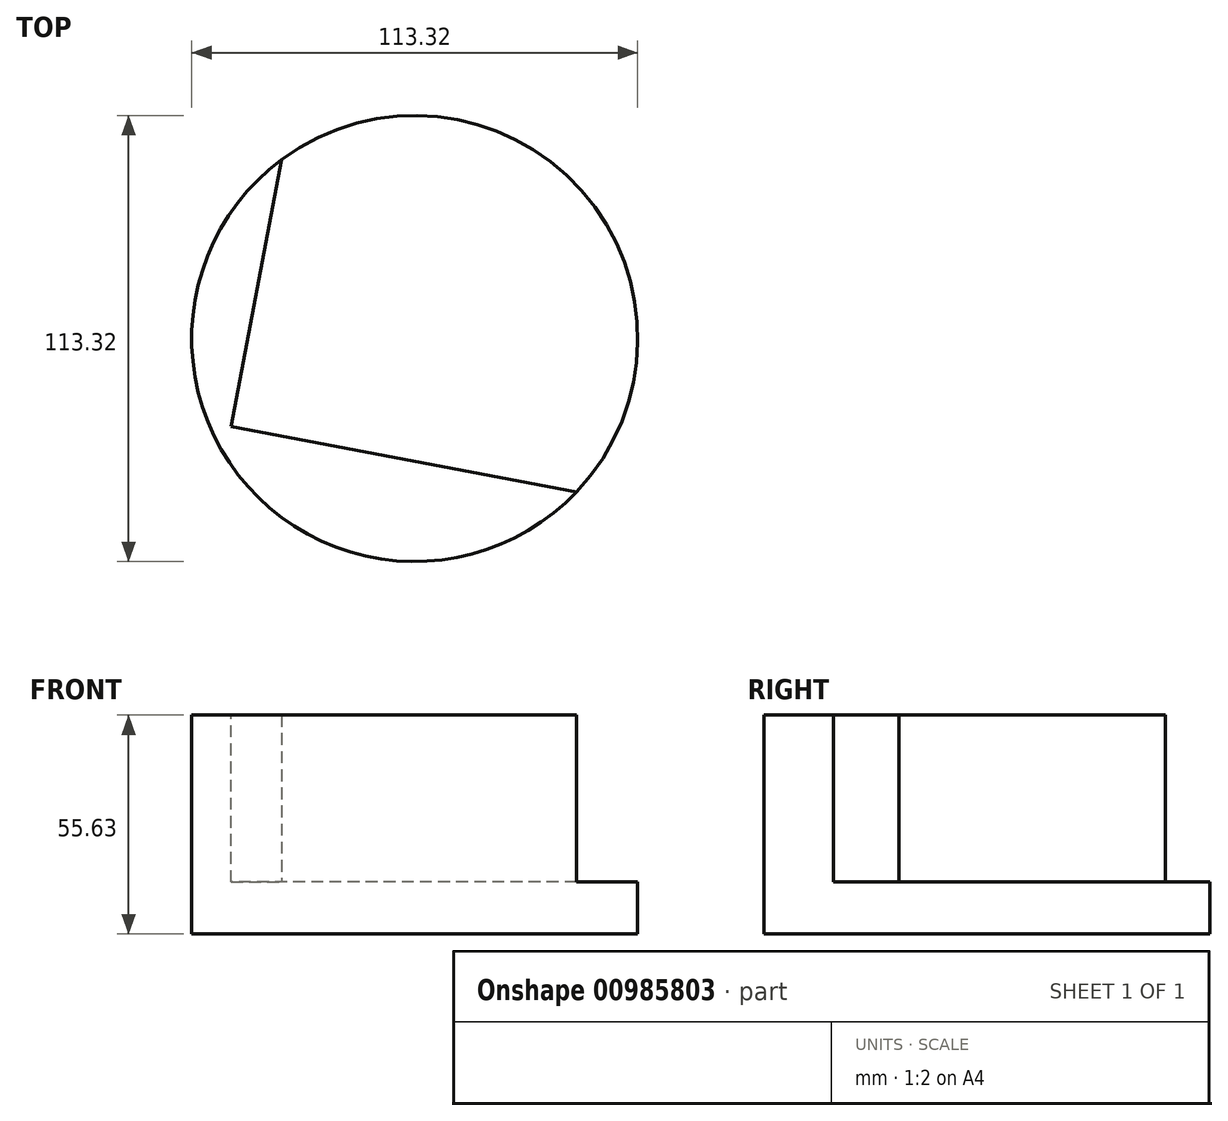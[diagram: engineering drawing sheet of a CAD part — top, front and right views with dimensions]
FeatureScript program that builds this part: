
annotation { "Feature Type Name" : "Feature", "Feature Type Description" : "" }
export const myFeature = defineFeature(function(context is Context, id is Id, definition is map)
    precondition{}
    {
        {
            var Q0;
            Q0=qCreatedBy(makeId("Top.planeOp"),FACE);
            var sketch = newSketch(context, id + "F0", { "sketchPlane" : qUnion([Q0])});
            skCircle(sketch, "E0", {"center": v(0, 0) * mm, "radius": 56.66 * mm});
            skSolve(sketch);
        }
        {
            var Q0;
            Q0 = qSketchRegion(id + "F0", true);
            extrude(context, id + "F1", {"entities" : qUnion([Q0]), "depth" : 55.63 * mm, "offsetDistance" : 25.4 * mm});
        }
        {
            var Q0;
            Q0=makeQuery(id+"F1.opExtrude","CAP_FACE",FACE,{"disambiguationData":[OSD([sQuery(id+"F0.wireOp",EDGE,"E0")])],"isStart":false});
            var sketch = newSketch(context, id + "F2", { "sketchPlane" : qUnion([Q0])});
            skCircle(sketch, "E1.cCircle", {"center": v(26.32, 27.41) * mm, "radius": 62.45 * mm, "construction": true});
            skLineSegment(sketch, "E1.0", {"start": v(76.07, -45.57) * mm, "end": v(-46.66, -22.33) * mm});
            skLineSegment(sketch, "E1.1", {"start": v(-46.66, -22.33) * mm, "end": v(-23.42, 100.4) * mm});
            skLineSegment(sketch, "E1.2", {"start": v(-23.42, 100.4) * mm, "end": v(99.3, 77.16) * mm});
            skLineSegment(sketch, "E1.3", {"start": v(99.3, 77.16) * mm, "end": v(76.07, -45.57) * mm});
            skPoint(sketch, "E1.0.midPoint", {"position": v(14.7, -33.95) * mm});
            skSolve(sketch);
        }
        {
            var Q0;
            {var subQ0=sQuery(id+"F2.wireOp",EDGE,"E1.2");Q0=makeQuery(id+"F2.imprint","IMPRINT",FACE,{"disambiguationData":[TD([[makeQuery(id+"F2.imprint","IMPRINT",EDGE,{"derivedFrom":subQ0}),-1.0]])]});}
            var Q1;
            {var subQ0=sQuery(id+"F2.wireOp",EDGE,"E1.1");var subQ1=sQuery(id+"F2.wireOp",EDGE,"E1.0");var subQ2=makeQuery(id+"F2.imprint","INTERSECT",VERTEX,{"derivedFrom":[subQ1,subQ0]});Q1=makeQuery(id+"F2.imprint","IMPRINT",FACE,{"disambiguationData":[TD([[makeQuery(id+"F2.imprint","IMPRINT",EDGE,{"disambiguationData":[TD([[subQ2,1.0]])],"derivedFrom":subQ1}),-1.0]])]});}
            extrude(context, id + "F3", {"entities" : qUnion([Q0, Q1]), "operationType" : NewBodyOperationType.REMOVE, "oppositeDirection" : true, "depth" : 42.42 * mm, "offsetDistance" : 25.4 * mm});
        }
    });
